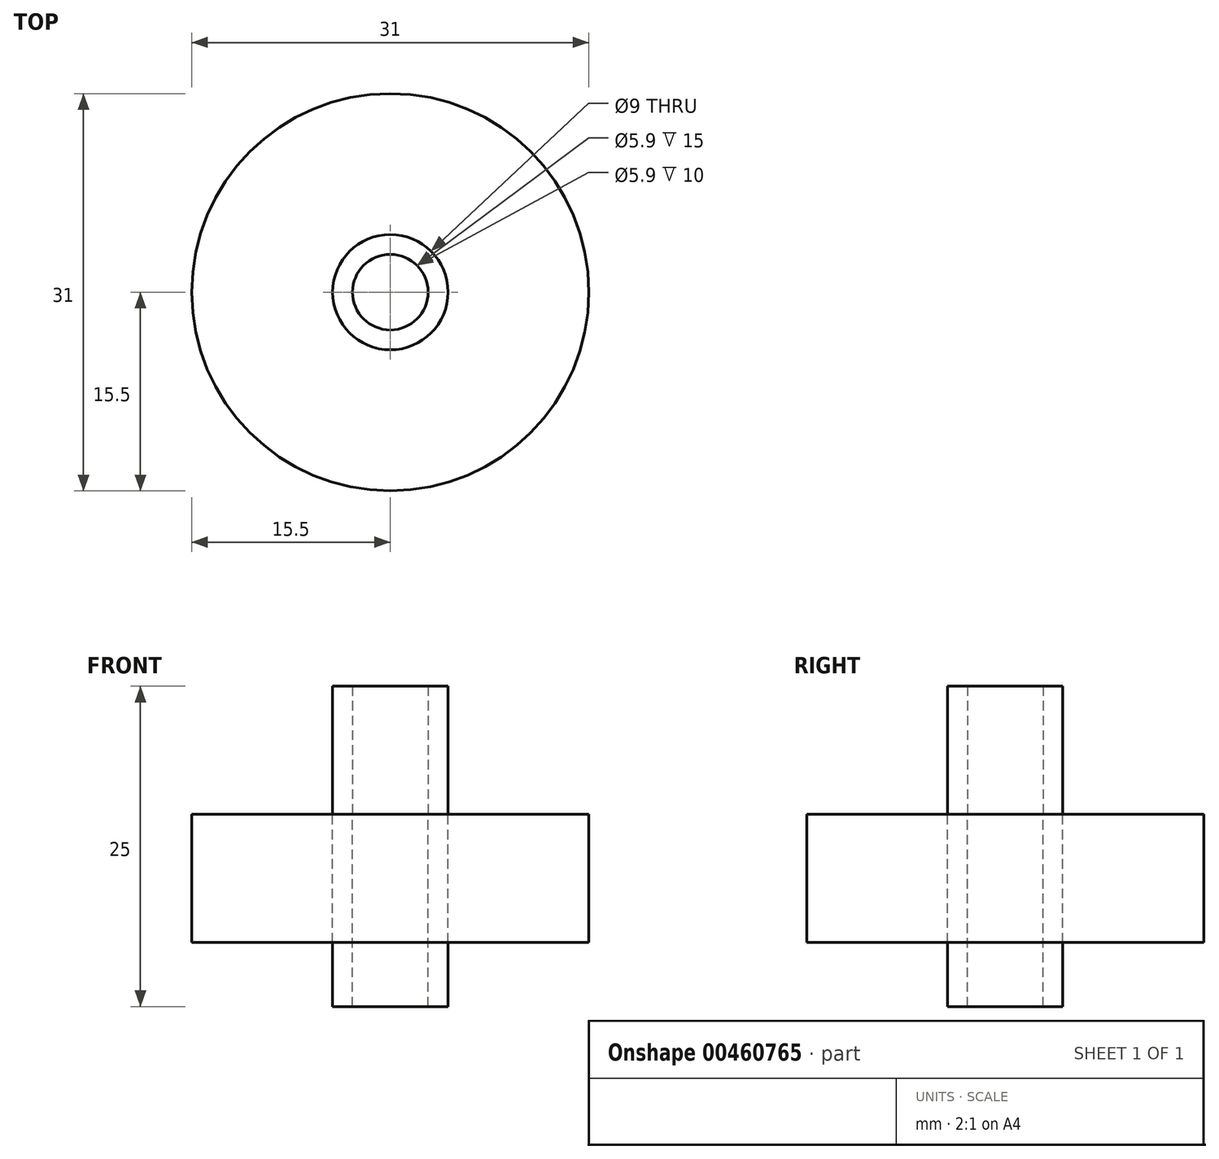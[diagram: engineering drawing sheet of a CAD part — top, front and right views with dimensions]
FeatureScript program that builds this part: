
annotation { "Feature Type Name" : "Feature", "Feature Type Description" : "" }
export const myFeature = defineFeature(function(context is Context, id is Id, definition is map)
    precondition{}
    {
        {
            var Q0;
            Q0=qCreatedBy(makeId("Top.planeOp"),FACE);
            var sketch = newSketch(context, id + "F0", { "sketchPlane" : qUnion([Q0])});
            skCircle(sketch, "E0", {"center": v(0, 0) * mm, "radius": 15.5 * mm});
            skCircle(sketch, "E1", {"center": v(0, 0) * mm, "radius": 4.5 * mm});
            skCircle(sketch, "E2", {"center": v(0, 0) * mm, "radius": 2.95 * mm});
            skSolve(sketch);
        }
        {
            var Q0;
            Q0=makeQuery(id+"F0.imprint","IMPRINT",FACE,{"disambiguationData":[TD([[makeQuery(id+"F0.imprint","IMPRINT",EDGE,{"derivedFrom":sQuery(id+"F0.wireOp",EDGE,"E1")}),1.0]])]});
            extrude(context, id + "F1", {"entities" : qUnion([Q0]), "depth" : 10 * mm});
        }
        {
            var Q0;
            Q0 = qSketchRegion(id + "F0", true);
            extrude(context, id + "F2", {"entities" : qUnion([Q0]), "oppositeDirection" : true, "depth" : 10 * mm});
        }
        {
            var Q0;
            Q0=makeQuery(id+"F1.opExtrude","CAP_FACE",FACE,{"disambiguationData":[OSD([sQuery(id+"F0.wireOp",EDGE,"E1"),sQuery(id+"F0.wireOp",EDGE,"E2")])],"isStart":true});
            extrude(context, id + "F3", {"entities" : qUnion([Q0]), "depth" : 15 * mm});
        }
    });
